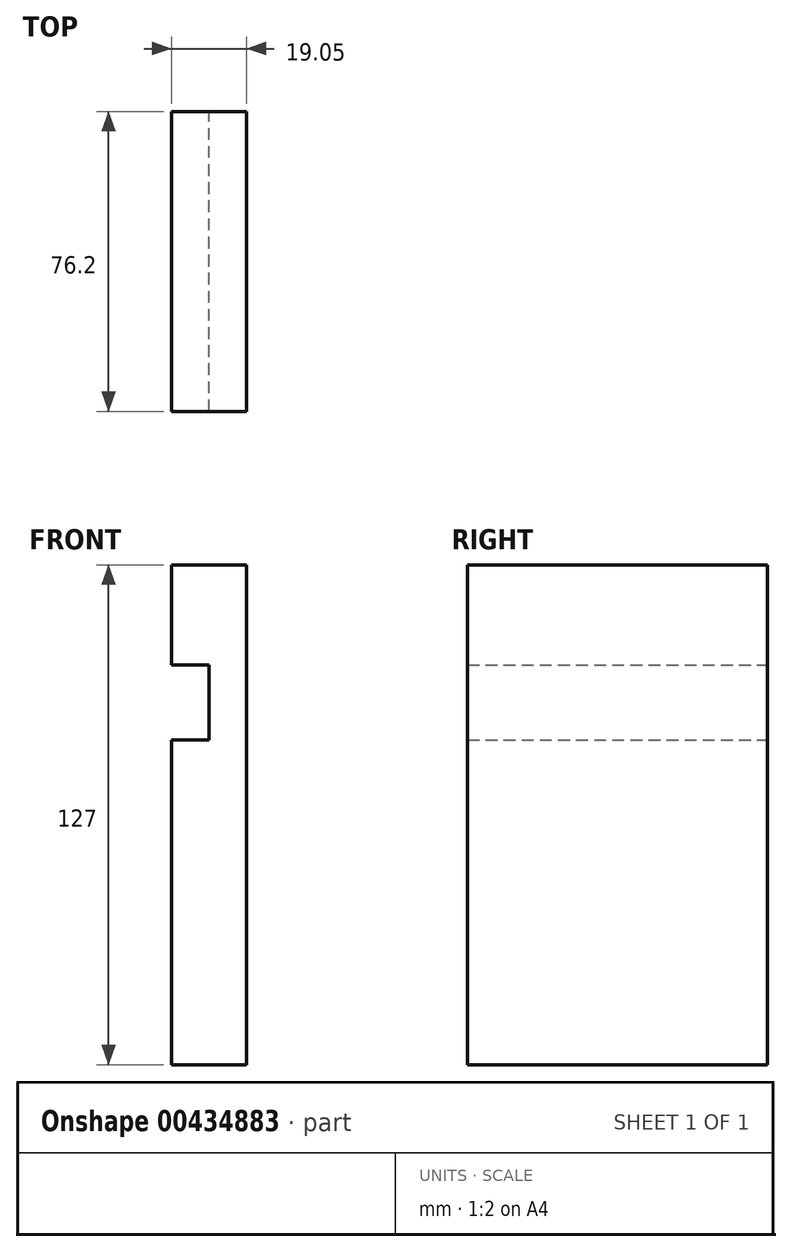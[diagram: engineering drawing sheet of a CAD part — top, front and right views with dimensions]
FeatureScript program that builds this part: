
annotation { "Feature Type Name" : "Feature", "Feature Type Description" : "" }
export const myFeature = defineFeature(function(context is Context, id is Id, definition is map)
    precondition{}
    {
        {
            var Q0;
            Q0=qCreatedBy(makeId("Front.planeOp"),FACE);
            var sketch = newSketch(context, id + "F0", { "sketchPlane" : qUnion([Q0])});
            skLineSegment(sketch, "E0", {"start": v(0, -52.02) * mm, "end": v(0, 74.98) * mm});
            skLineSegment(sketch, "E1", {"start": v(0, 74.98) * mm, "end": v(-19.05, 74.98) * mm});
            skLineSegment(sketch, "E2", {"start": v(-19.05, 74.98) * mm, "end": v(-19.05, 49.58) * mm});
            skLineSegment(sketch, "E3", {"start": v(-19.05, 49.58) * mm, "end": v(-9.53, 49.58) * mm});
            skPoint(sketch, "E3.endSnap0", {"position": v(-9.53, 74.98) * mm});
            skLineSegment(sketch, "E4", {"start": v(-9.53, 49.58) * mm, "end": v(-9.53, 30.53) * mm});
            skLineSegment(sketch, "E5", {"start": v(-9.53, 30.53) * mm, "end": v(-19.05, 30.53) * mm});
            skLineSegment(sketch, "E6", {"start": v(-19.05, 30.53) * mm, "end": v(-19.05, -52.02) * mm});
            skLineSegment(sketch, "E7", {"start": v(-19.05, -52.02) * mm, "end": v(0, -52.02) * mm});
            skSolve(sketch);
        }
        {
            var Q0;
            Q0 = qSketchRegion(id + "F0", true);
            extrude(context, id + "F1", {"entities" : qUnion([Q0]), "depth" : 76.2 * mm});
        }
    });
